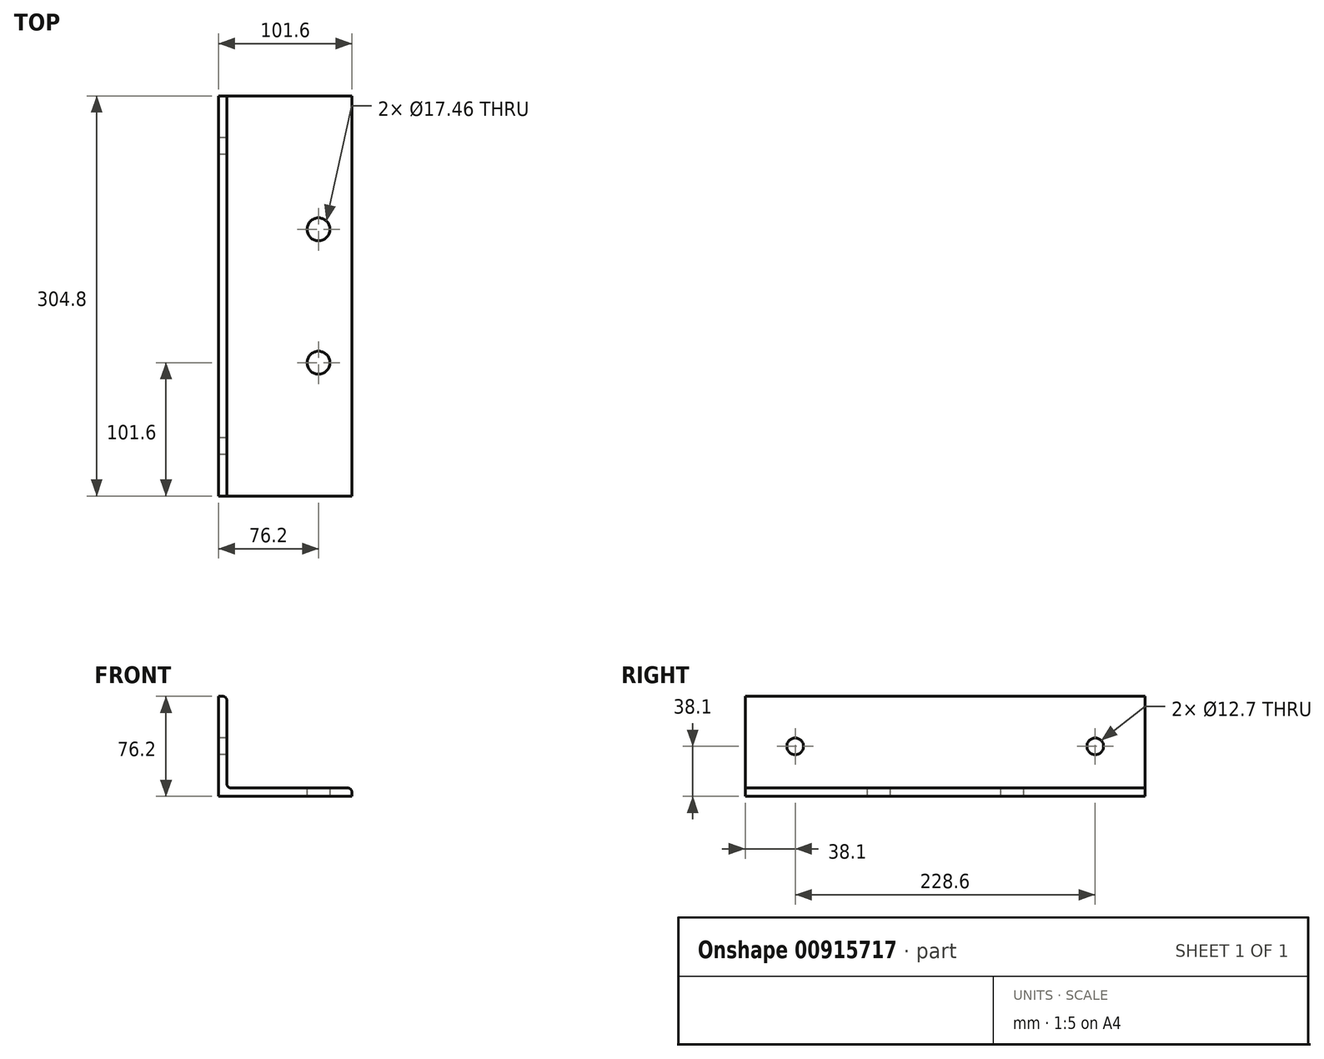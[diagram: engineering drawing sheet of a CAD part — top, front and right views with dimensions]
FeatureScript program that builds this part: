
annotation { "Feature Type Name" : "Feature", "Feature Type Description" : "" }
export const myFeature = defineFeature(function(context is Context, id is Id, definition is map)
    precondition{}
    {
        {
            var Q0;
            Q0=qCreatedBy(makeId("Front.planeOp"),FACE);
            var sketch = newSketch(context, id + "F0", { "sketchPlane" : qUnion([Q0])});
            skLineSegment(sketch, "E0", {"start": v(0, 76.2) * mm, "end": v(0, 0) * mm});
            skLineSegment(sketch, "E1", {"start": v(0, 0) * mm, "end": v(101.6, 0) * mm});
            skLineSegment(sketch, "E2", {"start": v(101.6, 0) * mm, "end": v(101.6, 3.17) * mm});
            skLineSegment(sketch, "E3", {"start": v(98.43, 6.35) * mm, "end": v(9.52, 6.35) * mm});
            skLineSegment(sketch, "E4", {"start": v(6.35, 9.52) * mm, "end": v(6.35, 73.03) * mm});
            skLineSegment(sketch, "E5", {"start": v(3.17, 76.2) * mm, "end": v(0, 76.2) * mm});
            skPoint(sketch, "E6.visualSharp", {"position": v(6.35, 6.35) * mm});
            skArc(sketch, "E6.filletArc", {"start": v(6.35, 9.52) * mm, "mid": v(7.28, 7.28) * mm, "end": v(9.52, 6.35) * mm});
            skPoint(sketch, "E7.visualSharp", {"position": v(6.35, 76.2) * mm});
            skArc(sketch, "E7.filletArc", {"start": v(6.35, 73.03) * mm, "mid": v(5.42, 75.27) * mm, "end": v(3.17, 76.2) * mm});
            skPoint(sketch, "E8.visualSharp", {"position": v(101.6, 6.35) * mm});
            skArc(sketch, "E8.filletArc", {"start": v(101.6, 3.17) * mm, "mid": v(100.67, 5.42) * mm, "end": v(98.43, 6.35) * mm});
            skSolve(sketch);
        }
        {
            var Q0;
            Q0=qSketchRegion(id+"F0",true);
            extrude(context, id + "F1", {"entities" : qUnion([Q0]), "depth" : 304.8 * mm, "offsetDistance" : 25.4 * mm, "symmetric" : true});
        }
        {
            var Q0;
            Q0=makeQuery(id+"F1.opExtrude","SWEPT_FACE",FACE,{"disambiguationData":[OSD([sQuery(id+"F0.wireOp",EDGE,"E1")])]});
            var sketch = newSketch(context, id + "F2", { "sketchPlane" : qUnion([Q0])});
            skCircle(sketch, "E9", {"center": v(76.2, 50.8) * mm, "radius": 8.73 * mm});
            skCircle(sketch, "E10", {"center": v(76.2, -50.8) * mm, "radius": 8.73 * mm});
            skLineSegment(sketch, "E11", {"start": v(0, 0) * mm, "end": v(101.6, 0) * mm, "construction": true});
            skSolve(sketch);
        }
        {
            var Q0;
            Q0 = qSketchRegion(id + "F2", true);
            extrude(context, id + "F3", {"entities" : qUnion([Q0]), "operationType" : NewBodyOperationType.REMOVE, "endBound" : BoundingType.THROUGH_ALL, "oppositeDirection" : true, "depth" : 25.4 * mm, "offsetDistance" : 25.4 * mm});
        }
        {
            var Q0;
            Q0=makeQuery(id+"F1.opExtrude","SWEPT_FACE",FACE,{"disambiguationData":[OSD([sQuery(id+"F0.wireOp",EDGE,"E0")])]});
            var sketch = newSketch(context, id + "F4", { "sketchPlane" : qUnion([Q0])});
            skCircle(sketch, "E12", {"center": v(-114.3, 38.1) * mm, "radius": 6.35 * mm});
            skCircle(sketch, "E13", {"center": v(114.3, 38.1) * mm, "radius": 6.35 * mm});
            skSolve(sketch);
        }
        {
            var Q0;
            Q0 = qSketchRegion(id + "F4", true);
            extrude(context, id + "F5", {"entities" : qUnion([Q0]), "operationType" : NewBodyOperationType.REMOVE, "endBound" : BoundingType.THROUGH_ALL, "oppositeDirection" : true, "depth" : 25.4 * mm, "offsetDistance" : 25.4 * mm});
        }
    });
